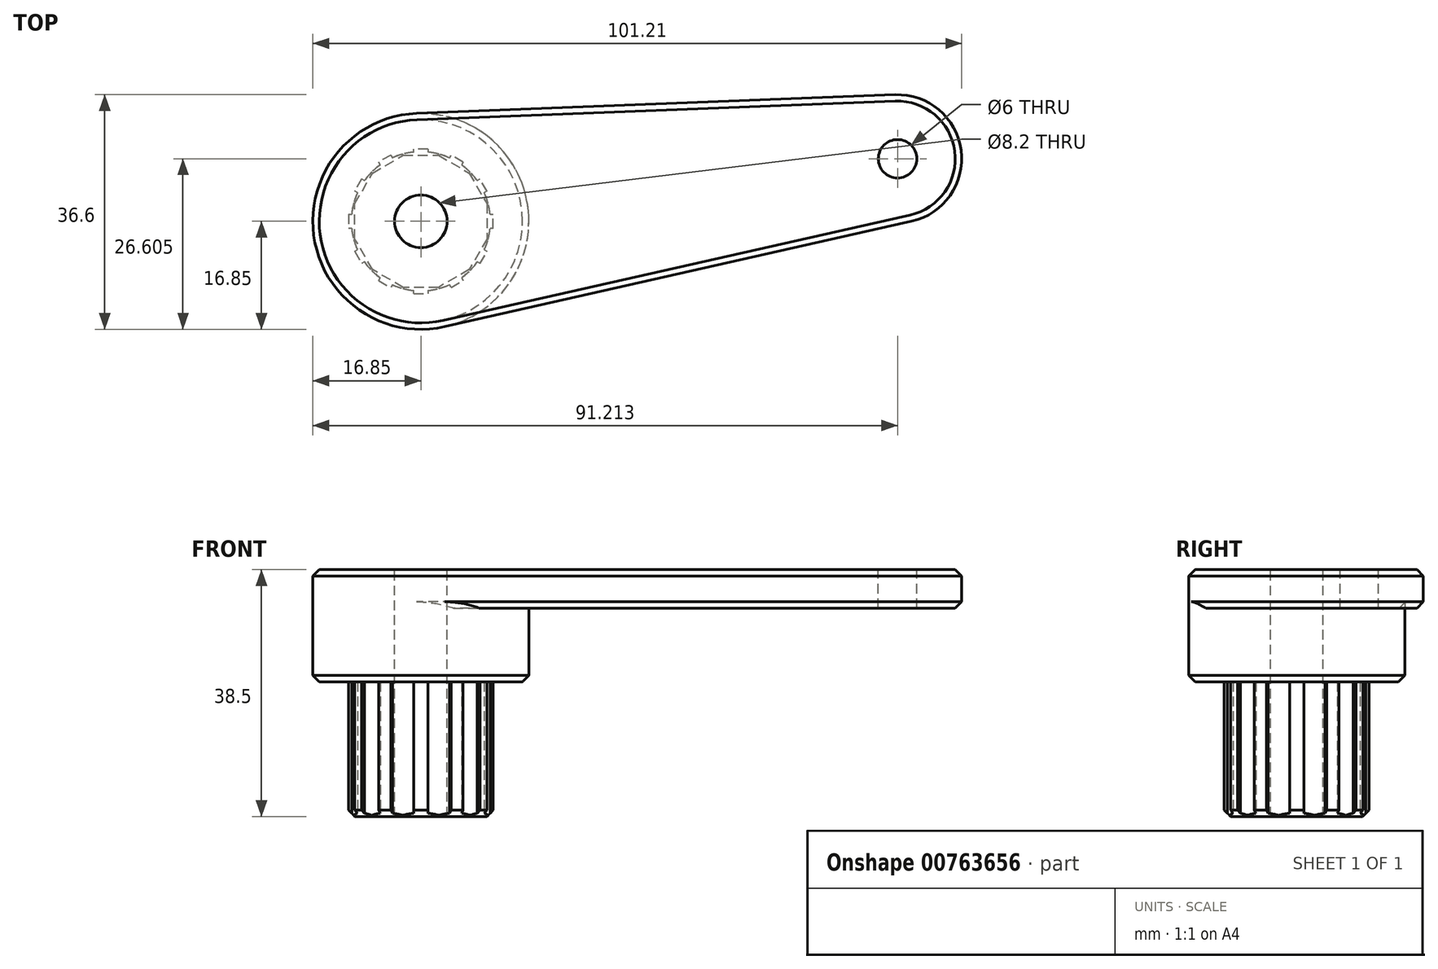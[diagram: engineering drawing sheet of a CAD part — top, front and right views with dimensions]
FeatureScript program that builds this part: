
annotation { "Feature Type Name" : "Feature", "Feature Type Description" : "" }
export const myFeature = defineFeature(function(context is Context, id is Id, definition is map)
    precondition{}
    {
        {
            var Q0;
            Q0=qCreatedBy(makeId("Top.planeOp"),FACE);
            var sketch = newSketch(context, id + "F0", { "sketchPlane" : qUnion([Q0])});
            skArc(sketch, "E0", {"start": v(-6.35, 8.8) * mm, "mid": v(-7.67, 7.67) * mm, "end": v(-8.8, 6.35) * mm});
            skLineSegment(sketch, "E1", {"start": v(0, 0) * mm, "end": v(0, 23.2) * mm, "construction": true});
            skLineSegment(sketch, "E2", {"start": v(-1.1, 10.8) * mm, "end": v(-1.1, 11.3) * mm});
            skLineSegment(sketch, "E3", {"start": v(-1.1, 11.3) * mm, "end": v(0, 11.3) * mm});
            skLineSegment(sketch, "E4.MirrorCS", {"start": v(1.1, 10.8) * mm, "end": v(1.1, 11.3) * mm});
            skLineSegment(sketch, "E5.MirrorCS", {"start": v(1.1, 11.3) * mm, "end": v(0, 11.3) * mm});
            skLineSegment(sketch, "E6.1.0", {"start": v(-6.35, 8.8) * mm, "end": v(-6.6, 9.23) * mm});
            skLineSegment(sketch, "E6.1.1", {"start": v(-6.6, 9.23) * mm, "end": v(-5.65, 9.78) * mm});
            skLineSegment(sketch, "E6.1.2", {"start": v(-4.7, 10.33) * mm, "end": v(-5.65, 9.78) * mm});
            skLineSegment(sketch, "E6.1.3", {"start": v(-4.44, 9.9) * mm, "end": v(-4.7, 10.33) * mm});
            skLineSegment(sketch, "E6.1.4", {"start": v(0, 0) * mm, "end": v(-11.6, 20.1) * mm, "construction": true});
            skLineSegment(sketch, "E6.2.0", {"start": v(-9.9, 4.44) * mm, "end": v(-10.33, 4.7) * mm});
            skLineSegment(sketch, "E6.2.1", {"start": v(-10.33, 4.7) * mm, "end": v(-9.78, 5.65) * mm});
            skLineSegment(sketch, "E6.2.2", {"start": v(-9.23, 6.6) * mm, "end": v(-9.78, 5.65) * mm});
            skLineSegment(sketch, "E6.2.3", {"start": v(-8.8, 6.35) * mm, "end": v(-9.23, 6.6) * mm});
            skLineSegment(sketch, "E6.2.4", {"start": v(0, 0) * mm, "end": v(-20.1, 11.6) * mm, "construction": true});
            skLineSegment(sketch, "E6.3.0", {"start": v(-10.8, -1.1) * mm, "end": v(-11.3, -1.1) * mm});
            skLineSegment(sketch, "E6.3.1", {"start": v(-11.3, -1.1) * mm, "end": v(-11.3, 0) * mm});
            skLineSegment(sketch, "E6.3.2", {"start": v(-11.3, 1.1) * mm, "end": v(-11.3, 0) * mm});
            skLineSegment(sketch, "E6.3.3", {"start": v(-10.8, 1.1) * mm, "end": v(-11.3, 1.1) * mm});
            skLineSegment(sketch, "E6.3.4", {"start": v(0, 0) * mm, "end": v(-23.2, 0) * mm, "construction": true});
            skLineSegment(sketch, "E6.4.0", {"start": v(-8.8, -6.35) * mm, "end": v(-9.23, -6.6) * mm});
            skLineSegment(sketch, "E6.4.1", {"start": v(-9.23, -6.6) * mm, "end": v(-9.78, -5.65) * mm});
            skLineSegment(sketch, "E6.4.2", {"start": v(-10.33, -4.7) * mm, "end": v(-9.78, -5.65) * mm});
            skLineSegment(sketch, "E6.4.3", {"start": v(-9.9, -4.44) * mm, "end": v(-10.33, -4.7) * mm});
            skLineSegment(sketch, "E6.4.4", {"start": v(0, 0) * mm, "end": v(-20.1, -11.6) * mm, "construction": true});
            skLineSegment(sketch, "E6.5.0", {"start": v(-4.44, -9.9) * mm, "end": v(-4.7, -10.33) * mm});
            skLineSegment(sketch, "E6.5.1", {"start": v(-4.7, -10.33) * mm, "end": v(-5.65, -9.78) * mm});
            skLineSegment(sketch, "E6.5.2", {"start": v(-6.6, -9.23) * mm, "end": v(-5.65, -9.78) * mm});
            skLineSegment(sketch, "E6.5.3", {"start": v(-6.35, -8.8) * mm, "end": v(-6.6, -9.23) * mm});
            skLineSegment(sketch, "E6.5.4", {"start": v(0, 0) * mm, "end": v(-11.6, -20.1) * mm, "construction": true});
            skLineSegment(sketch, "E6.6.0", {"start": v(1.1, -10.8) * mm, "end": v(1.1, -11.3) * mm});
            skLineSegment(sketch, "E6.6.1", {"start": v(1.1, -11.3) * mm, "end": v(0, -11.3) * mm});
            skLineSegment(sketch, "E6.6.2", {"start": v(-1.1, -11.3) * mm, "end": v(0, -11.3) * mm});
            skLineSegment(sketch, "E6.6.3", {"start": v(-1.1, -10.8) * mm, "end": v(-1.1, -11.3) * mm});
            skLineSegment(sketch, "E6.6.4", {"start": v(0, 0) * mm, "end": v(0, -23.2) * mm, "construction": true});
            skLineSegment(sketch, "E6.7.0", {"start": v(6.35, -8.8) * mm, "end": v(6.6, -9.23) * mm});
            skLineSegment(sketch, "E6.7.1", {"start": v(6.6, -9.23) * mm, "end": v(5.65, -9.78) * mm});
            skLineSegment(sketch, "E6.7.2", {"start": v(4.7, -10.33) * mm, "end": v(5.65, -9.78) * mm});
            skLineSegment(sketch, "E6.7.3", {"start": v(4.44, -9.9) * mm, "end": v(4.7, -10.33) * mm});
            skLineSegment(sketch, "E6.7.4", {"start": v(0, 0) * mm, "end": v(11.6, -20.1) * mm, "construction": true});
            skLineSegment(sketch, "E6.8.0", {"start": v(9.9, -4.44) * mm, "end": v(10.33, -4.7) * mm});
            skLineSegment(sketch, "E6.8.1", {"start": v(10.33, -4.7) * mm, "end": v(9.78, -5.65) * mm});
            skLineSegment(sketch, "E6.8.2", {"start": v(9.23, -6.6) * mm, "end": v(9.78, -5.65) * mm});
            skLineSegment(sketch, "E6.8.3", {"start": v(8.8, -6.35) * mm, "end": v(9.23, -6.6) * mm});
            skLineSegment(sketch, "E6.8.4", {"start": v(0, 0) * mm, "end": v(20.1, -11.6) * mm, "construction": true});
            skLineSegment(sketch, "E6.9.0", {"start": v(10.8, 1.1) * mm, "end": v(11.3, 1.1) * mm});
            skLineSegment(sketch, "E6.9.1", {"start": v(11.3, 1.1) * mm, "end": v(11.3, 0) * mm});
            skLineSegment(sketch, "E6.9.2", {"start": v(11.3, -1.1) * mm, "end": v(11.3, 0) * mm});
            skLineSegment(sketch, "E6.9.3", {"start": v(10.8, -1.1) * mm, "end": v(11.3, -1.1) * mm});
            skLineSegment(sketch, "E6.9.4", {"start": v(0, 0) * mm, "end": v(23.2, 0) * mm, "construction": true});
            skLineSegment(sketch, "E6.10.0", {"start": v(8.8, 6.35) * mm, "end": v(9.23, 6.6) * mm});
            skLineSegment(sketch, "E6.10.1", {"start": v(9.23, 6.6) * mm, "end": v(9.78, 5.65) * mm});
            skLineSegment(sketch, "E6.10.2", {"start": v(10.33, 4.7) * mm, "end": v(9.78, 5.65) * mm});
            skLineSegment(sketch, "E6.10.3", {"start": v(9.9, 4.44) * mm, "end": v(10.33, 4.7) * mm});
            skLineSegment(sketch, "E6.10.4", {"start": v(0, 0) * mm, "end": v(20.1, 11.6) * mm, "construction": true});
            skLineSegment(sketch, "E6.11.0", {"start": v(4.44, 9.9) * mm, "end": v(4.7, 10.33) * mm});
            skLineSegment(sketch, "E6.11.1", {"start": v(4.7, 10.33) * mm, "end": v(5.65, 9.78) * mm});
            skLineSegment(sketch, "E6.11.2", {"start": v(6.6, 9.23) * mm, "end": v(5.65, 9.78) * mm});
            skLineSegment(sketch, "E6.11.3", {"start": v(6.35, 8.8) * mm, "end": v(6.6, 9.23) * mm});
            skLineSegment(sketch, "E6.11.4", {"start": v(0, 0) * mm, "end": v(11.6, 20.1) * mm, "construction": true});
            skArc(sketch, "E7.trimOffspring", {"start": v(-1.1, 10.8) * mm, "mid": v(-2.8, 10.48) * mm, "end": v(-4.44, 9.9) * mm});
            skArc(sketch, "E8.trimOffspring", {"start": v(4.44, 9.9) * mm, "mid": v(2.8, 10.48) * mm, "end": v(1.1, 10.8) * mm});
            skArc(sketch, "E9.trimOffspring", {"start": v(8.8, 6.35) * mm, "mid": v(7.67, 7.67) * mm, "end": v(6.35, 8.8) * mm});
            skArc(sketch, "E10.trimOffspring", {"start": v(10.8, 1.1) * mm, "mid": v(10.48, 2.8) * mm, "end": v(9.9, 4.44) * mm});
            skArc(sketch, "E11.trimOffspring", {"start": v(9.9, -4.44) * mm, "mid": v(10.48, -2.8) * mm, "end": v(10.8, -1.1) * mm});
            skArc(sketch, "E12.trimOffspring", {"start": v(6.35, -8.8) * mm, "mid": v(7.67, -7.67) * mm, "end": v(8.8, -6.35) * mm});
            skArc(sketch, "E13.trimOffspring", {"start": v(1.1, -10.8) * mm, "mid": v(2.8, -10.48) * mm, "end": v(4.44, -9.9) * mm});
            skArc(sketch, "E14.trimOffspring", {"start": v(-4.44, -9.9) * mm, "mid": v(-2.8, -10.48) * mm, "end": v(-1.1, -10.8) * mm});
            skArc(sketch, "E15.trimOffspring", {"start": v(-8.8, -6.35) * mm, "mid": v(-7.67, -7.67) * mm, "end": v(-6.35, -8.8) * mm});
            skArc(sketch, "E16.trimOffspring", {"start": v(-10.8, -1.1) * mm, "mid": v(-10.48, -2.8) * mm, "end": v(-9.9, -4.44) * mm});
            skArc(sketch, "E17.trimOffspring", {"start": v(-9.9, 4.44) * mm, "mid": v(-10.48, 2.8) * mm, "end": v(-10.8, 1.1) * mm});
            skSolve(sketch);
        }
        {
            var Q0;
            Q0 = qSketchRegion(id + "F0", true);
            extrude(context, id + "F1", {"entities" : qUnion([Q0]), "depth" : 21 * mm, "offsetDistance" : 25 * mm});
        }
        {
            var Q0;
            Q0=makeQuery(id+"F1.opExtrude","CAP_FACE",FACE,{"disambiguationData":[OSD([sQuery(id+"F0.wireOp",EDGE,"E0"),sQuery(id+"F0.wireOp",EDGE,"E2"),sQuery(id+"F0.wireOp",EDGE,"E3"),sQuery(id+"F0.wireOp",EDGE,"E4.MirrorCS"),sQuery(id+"F0.wireOp",EDGE,"E5.MirrorCS"),sQuery(id+"F0.wireOp",EDGE,"E6.1.0"),sQuery(id+"F0.wireOp",EDGE,"E6.1.1"),sQuery(id+"F0.wireOp",EDGE,"E6.1.2"),sQuery(id+"F0.wireOp",EDGE,"E6.1.3"),sQuery(id+"F0.wireOp",EDGE,"E6.2.0"),sQuery(id+"F0.wireOp",EDGE,"E6.2.1"),sQuery(id+"F0.wireOp",EDGE,"E6.2.2"),sQuery(id+"F0.wireOp",EDGE,"E6.2.3"),sQuery(id+"F0.wireOp",EDGE,"E6.3.0"),sQuery(id+"F0.wireOp",EDGE,"E6.3.1"),sQuery(id+"F0.wireOp",EDGE,"E6.3.2"),sQuery(id+"F0.wireOp",EDGE,"E6.3.3"),sQuery(id+"F0.wireOp",EDGE,"E6.4.0"),sQuery(id+"F0.wireOp",EDGE,"E6.4.1"),sQuery(id+"F0.wireOp",EDGE,"E6.4.2"),sQuery(id+"F0.wireOp",EDGE,"E6.4.3"),sQuery(id+"F0.wireOp",EDGE,"E6.5.0"),sQuery(id+"F0.wireOp",EDGE,"E6.5.1"),sQuery(id+"F0.wireOp",EDGE,"E6.5.2"),sQuery(id+"F0.wireOp",EDGE,"E6.5.3"),sQuery(id+"F0.wireOp",EDGE,"E6.6.0"),sQuery(id+"F0.wireOp",EDGE,"E6.6.1"),sQuery(id+"F0.wireOp",EDGE,"E6.6.2"),sQuery(id+"F0.wireOp",EDGE,"E6.6.3"),sQuery(id+"F0.wireOp",EDGE,"E6.7.0"),sQuery(id+"F0.wireOp",EDGE,"E6.7.1"),sQuery(id+"F0.wireOp",EDGE,"E6.7.2"),sQuery(id+"F0.wireOp",EDGE,"E6.7.3"),sQuery(id+"F0.wireOp",EDGE,"E6.8.0"),sQuery(id+"F0.wireOp",EDGE,"E6.8.1"),sQuery(id+"F0.wireOp",EDGE,"E6.8.2"),sQuery(id+"F0.wireOp",EDGE,"E6.8.3"),sQuery(id+"F0.wireOp",EDGE,"E6.9.0"),sQuery(id+"F0.wireOp",EDGE,"E6.9.1"),sQuery(id+"F0.wireOp",EDGE,"E6.9.2"),sQuery(id+"F0.wireOp",EDGE,"E6.9.3"),sQuery(id+"F0.wireOp",EDGE,"E6.10.0"),sQuery(id+"F0.wireOp",EDGE,"E6.10.1"),sQuery(id+"F0.wireOp",EDGE,"E6.10.2"),sQuery(id+"F0.wireOp",EDGE,"E6.10.3"),sQuery(id+"F0.wireOp",EDGE,"E6.11.0"),sQuery(id+"F0.wireOp",EDGE,"E6.11.1"),sQuery(id+"F0.wireOp",EDGE,"E6.11.2"),sQuery(id+"F0.wireOp",EDGE,"E6.11.3"),sQuery(id+"F0.wireOp",EDGE,"E7.trimOffspring"),sQuery(id+"F0.wireOp",EDGE,"E8.trimOffspring"),sQuery(id+"F0.wireOp",EDGE,"E9.trimOffspring"),sQuery(id+"F0.wireOp",EDGE,"E10.trimOffspring"),sQuery(id+"F0.wireOp",EDGE,"E11.trimOffspring"),sQuery(id+"F0.wireOp",EDGE,"E12.trimOffspring"),sQuery(id+"F0.wireOp",EDGE,"E13.trimOffspring"),sQuery(id+"F0.wireOp",EDGE,"E14.trimOffspring"),sQuery(id+"F0.wireOp",EDGE,"E15.trimOffspring"),sQuery(id+"F0.wireOp",EDGE,"E16.trimOffspring"),sQuery(id+"F0.wireOp",EDGE,"E17.trimOffspring"),sQuery(id+"F0.wireOp",EDGE,"FxzRTCrc-x6WC-5BfY-iGxO-CmnbOM1jqdhE")])],"isStart":false});
            var sketch = newSketch(context, id + "F2", { "sketchPlane" : qUnion([Q0])});
            skCircle(sketch, "E18", {"center": v(0, 0) * mm, "radius": 16.85 * mm});
            skSolve(sketch);
        }
        {
            var Q0;
            Q0 = qSketchRegion(id + "F2", true);
            extrude(context, id + "F3", {"entities" : qUnion([Q0]), "operationType" : NewBodyOperationType.ADD, "depth" : 17.5 * mm, "offsetDistance" : 25 * mm});
        }
        {
            var Q0;
            Q0=makeQuery(id+"F3.opExtrude","CAP_FACE",FACE,{"disambiguationData":[OSD([sQuery(id+"F2.wireOp",EDGE,"E18")])],"isStart":false});
            var sketch = newSketch(context, id + "F4", { "sketchPlane" : qUnion([Q0])});
            skCircle(sketch, "E19", {"center": v(0, 0) * mm, "radius": 4.1 * mm});
            skSolve(sketch);
        }
        {
            var Q0;
            Q0=makeQuery(id+"F3.opExtrude","CAP_EDGE",EDGE,{"disambiguationData":[OSD([sQuery(id+"F2.wireOp",EDGE,"E18")])],"isStart":true});
            var Q1;
            Q1=makeQuery(id+"F1.opExtrude","CAP_EDGE",EDGE,{"disambiguationData":[OSD([sQuery(id+"F0.wireOp",EDGE,"E6.2.1"),sQuery(id+"F0.wireOp",EDGE,"E6.2.2")])],"isStart":true});
            var Q2;
            Q2=makeQuery(id+"F1.opExtrude","CAP_EDGE",EDGE,{"disambiguationData":[OSD([sQuery(id+"F0.wireOp",EDGE,"E6.1.1"),sQuery(id+"F0.wireOp",EDGE,"E6.1.2")])],"isStart":true});
            var Q3;
            Q3=makeQuery(id+"F1.opExtrude","CAP_EDGE",EDGE,{"disambiguationData":[OSD([sQuery(id+"F0.wireOp",EDGE,"E6.3.1"),sQuery(id+"F0.wireOp",EDGE,"E6.3.2")])],"isStart":true});
            var Q4;
            Q4=makeQuery(id+"F1.opExtrude","CAP_EDGE",EDGE,{"disambiguationData":[OSD([sQuery(id+"F0.wireOp",EDGE,"E6.4.1"),sQuery(id+"F0.wireOp",EDGE,"E6.4.2")])],"isStart":true});
            var Q5;
            Q5=makeQuery(id+"F1.opExtrude","CAP_EDGE",EDGE,{"disambiguationData":[OSD([sQuery(id+"F0.wireOp",EDGE,"E6.5.1"),sQuery(id+"F0.wireOp",EDGE,"E6.5.2")])],"isStart":true});
            var Q6;
            Q6=makeQuery(id+"F1.opExtrude","CAP_EDGE",EDGE,{"disambiguationData":[OSD([sQuery(id+"F0.wireOp",EDGE,"E6.6.1"),sQuery(id+"F0.wireOp",EDGE,"E6.6.2")])],"isStart":true});
            var Q7;
            Q7=makeQuery(id+"F1.opExtrude","CAP_EDGE",EDGE,{"disambiguationData":[OSD([sQuery(id+"F0.wireOp",EDGE,"E6.7.1"),sQuery(id+"F0.wireOp",EDGE,"E6.7.2")])],"isStart":true});
            var Q8;
            Q8=makeQuery(id+"F1.opExtrude","CAP_EDGE",EDGE,{"disambiguationData":[OSD([sQuery(id+"F0.wireOp",EDGE,"E6.8.1"),sQuery(id+"F0.wireOp",EDGE,"E6.8.2")])],"isStart":true});
            var Q9;
            Q9=makeQuery(id+"F1.opExtrude","CAP_EDGE",EDGE,{"disambiguationData":[OSD([sQuery(id+"F0.wireOp",EDGE,"E6.9.1"),sQuery(id+"F0.wireOp",EDGE,"E6.9.2")])],"isStart":true});
            var Q10;
            Q10=makeQuery(id+"F1.opExtrude","CAP_EDGE",EDGE,{"disambiguationData":[OSD([sQuery(id+"F0.wireOp",EDGE,"E6.10.1"),sQuery(id+"F0.wireOp",EDGE,"E6.10.2")])],"isStart":true});
            var Q11;
            Q11=makeQuery(id+"F1.opExtrude","CAP_EDGE",EDGE,{"disambiguationData":[OSD([sQuery(id+"F0.wireOp",EDGE,"E6.11.1"),sQuery(id+"F0.wireOp",EDGE,"E6.11.2")])],"isStart":true});
            var Q12;
            Q12=makeQuery(id+"F1.opExtrude","CAP_EDGE",EDGE,{"disambiguationData":[OSD([sQuery(id+"F0.wireOp",EDGE,"E3"),sQuery(id+"F0.wireOp",EDGE,"E5.MirrorCS")])],"isStart":true});
            chamfer(context, id + "F5", {"entities" : qUnion([Q0, Q1, Q2, Q3, Q4, Q5, Q6, Q7, Q8, Q9, Q10, Q11, Q12]), "width" : 1 * mm, "tangentPropagation" : true});
        }
        {
            var Q0;
            Q0=makeQuery(id+"F3.opExtrude","CAP_FACE",FACE,{"disambiguationData":[OSD([sQuery(id+"F2.wireOp",EDGE,"E18")])],"isStart":false});
            var sketch = newSketch(context, id + "F6", { "sketchPlane" : qUnion([Q0])});
            skArc(sketch, "E20", {"start": v(76.56, 0) * mm, "mid": v(84.28, 11.06) * mm, "end": v(73.97, 19.75) * mm});
            skLineSegment(sketch, "E21", {"start": v(0, 0) * mm, "end": v(74.36, 9.75) * mm, "construction": true});
            skCircle(sketch, "E22", {"center": v(74.36, 9.75) * mm, "radius": 3 * mm});
            skLineSegment(sketch, "E23", {"start": v(76.56, 0) * mm, "end": v(3.7, -16.44) * mm});
            skCircle(sketch, "E24.0", {"center": v(0, 0) * mm, "radius": 16.85 * mm});
            skLineSegment(sketch, "E25", {"start": v(73.97, 19.75) * mm, "end": v(-0.66, 16.84) * mm});
            skSolve(sketch);
        }
        {
            var Q0;
            Q0 = qSketchRegion(id + "F6", true);
            extrude(context, id + "F7", {"entities" : qUnion([Q0]), "operationType" : NewBodyOperationType.ADD, "oppositeDirection" : true, "depth" : 6 * mm, "offsetDistance" : 25 * mm});
        }
        {
            var Q0;
            Q0 = qSketchRegion(id + "F4", true);
            extrude(context, id + "F8", {"entities" : qUnion([Q0]), "operationType" : NewBodyOperationType.REMOVE, "endBound" : BoundingType.UP_TO_NEXT, "oppositeDirection" : true, "depth" : 25 * mm, "offsetDistance" : 25 * mm});
        }
        {
            var Q0;
            Q0=makeQuery(id+"F7.boolean.opBoolean","MERGE",FACE,{"derivedFrom":[makeQuery(id+"F3.opExtrude","CAP_FACE",FACE,{"disambiguationData":[OSD([sQuery(id+"F2.wireOp",EDGE,"E18")])],"isStart":false}),makeQuery(id+"F7.opExtrude","CAP_FACE",FACE,{"disambiguationData":[OSD([sQuery(id+"F6.wireOp",EDGE,"E20"),sQuery(id+"F6.wireOp",EDGE,"E22"),sQuery(id+"F6.wireOp",EDGE,"E23"),sQuery(id+"F6.wireOp",EDGE,"E24.0"),sQuery(id+"F6.wireOp",EDGE,"E25")])],"isStart":true})]});
            var sketch = newSketch(context, id + "F9", { "sketchPlane" : qUnion([Q0])});
            skLineSegment(sketch, "E26.bottom", {"start": v(-62.17, 71.46) * mm, "end": v(104.94, 71.46) * mm});
            skLineSegment(sketch, "E26.top", {"start": v(-62.17, -49.24) * mm, "end": v(104.94, -49.24) * mm});
            skLineSegment(sketch, "E26.left", {"start": v(-62.17, 71.46) * mm, "end": v(-62.17, -49.24) * mm});
            skLineSegment(sketch, "E26.right", {"start": v(104.94, 71.46) * mm, "end": v(104.94, -49.24) * mm});
            skSolve(sketch);
        }
        {
            var Q0;
            Q0=makeQuery(id+"F7.opExtrude","CAP_EDGE",EDGE,{"disambiguationData":[OSD([sQuery(id+"F6.wireOp",EDGE,"E23")])],"isStart":true});
            var Q1;
            Q1=makeQuery(id+"F7.opExtrude","CAP_EDGE",EDGE,{"disambiguationData":[OSD([sQuery(id+"F6.wireOp",EDGE,"E23")])],"isStart":false});
            var Q2;
            Q2=makeQuery(id+"FavW1kSOJBTbv7q_1.boolean.opBoolean","INTERSECT",EDGE,{"derivedFrom":[makeQuery(id+"F7.opExtrude","SWEPT_FACE",FACE,{"disambiguationData":[OSD([sQuery(id+"F6.wireOp",EDGE,"E23")])]}),makeQuery(id+"FavW1kSOJBTbv7q_1.opExtrude","CAP_FACE",FACE,{"disambiguationData":[OSD([sQuery(id+"F9.wireOp",EDGE,"E26.bottom"),sQuery(id+"F9.wireOp",EDGE,"E26.top"),sQuery(id+"F9.wireOp",EDGE,"E26.left"),sQuery(id+"F9.wireOp",EDGE,"E26.right")])],"isStart":false})]});
            chamfer(context, id + "F10", {"entities" : qUnion([Q0, Q1, Q2]), "width" : 1 * mm, "tangentPropagation" : true});
        }
    });
